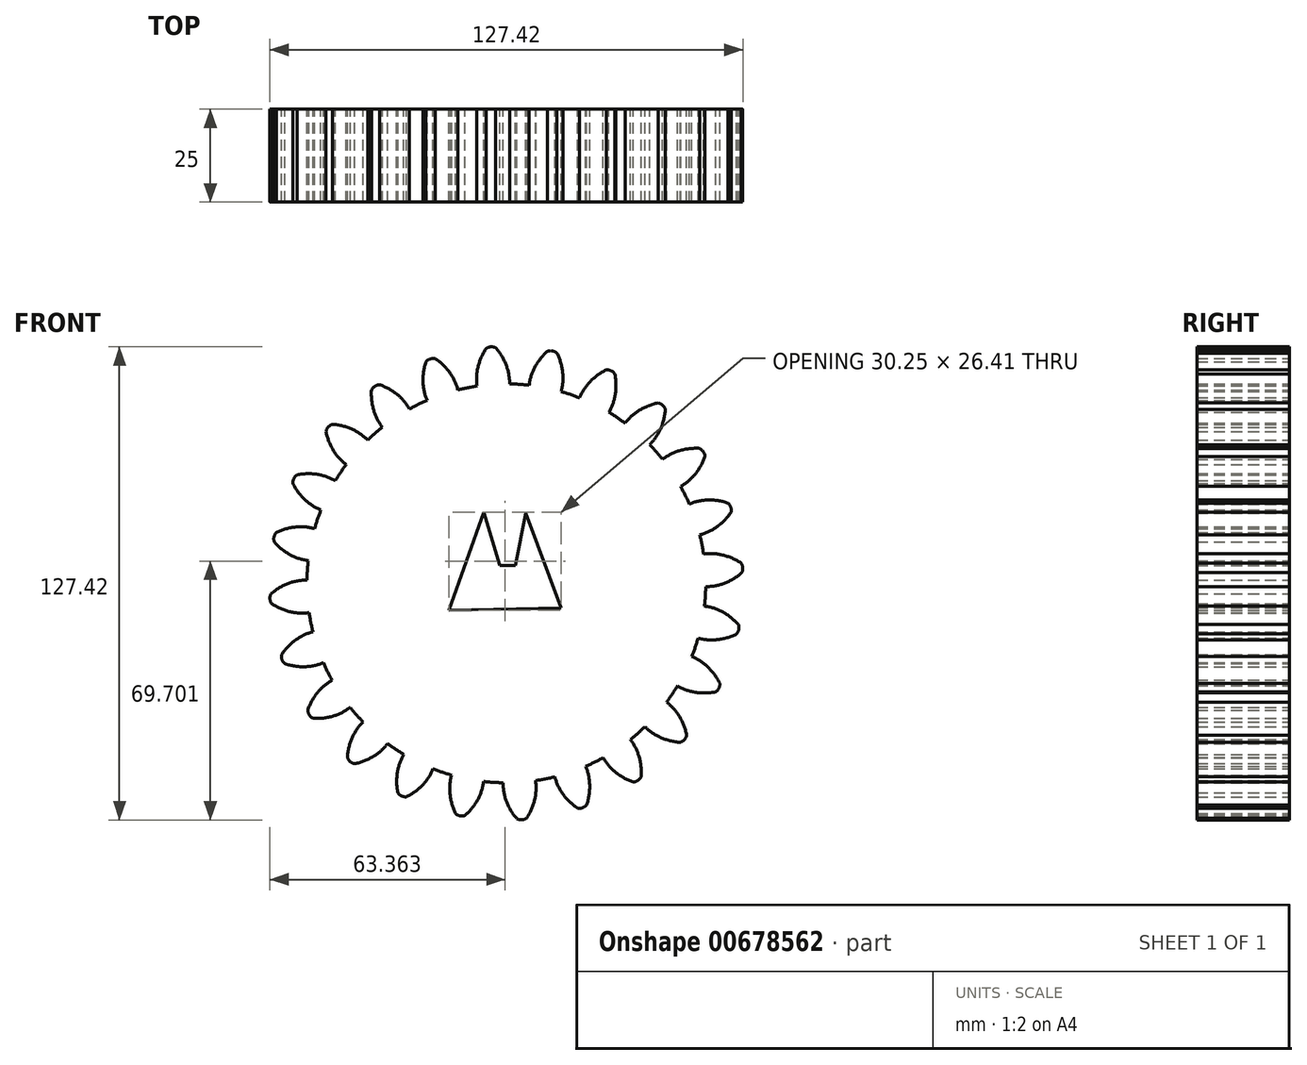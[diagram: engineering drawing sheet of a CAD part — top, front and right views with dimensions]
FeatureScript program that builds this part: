
annotation { "Feature Type Name" : "Feature", "Feature Type Description" : "" }
export const myFeature = defineFeature(function(context is Context, id is Id, definition is map)
    precondition{}
    {
        {
            var Q0;
            Q0=qCreatedBy(makeId("Front.planeOp"),FACE);
            var sketch = newSketch(context, id + "F0", { "sketchPlane" : qUnion([Q0])});
            skCircle(sketch, "E0", {"center": v(0, 0) * mm, "radius": 53.72 * mm});
            skCircle(sketch, "E1", {"center": v(0, 0) * mm, "radius": 58.67 * mm, "construction": true});
            skCircle(sketch, "E2", {"center": v(0, 0) * mm, "radius": 63.5 * mm, "construction": true});
            skLineSegment(sketch, "E3", {"start": v(0, 58.67) * mm, "end": v(-81.07, 58.67) * mm, "construction": true});
            skLineSegment(sketch, "E4", {"start": v(0, 58.67) * mm, "end": v(-75.05, 31.36) * mm, "construction": true});
            skCircle(sketch, "E5", {"center": v(0, 0) * mm, "radius": 55.14 * mm, "construction": true});
            skLineSegment(sketch, "E6", {"start": v(0, 0) * mm, "end": v(-5.28, 80.55) * mm, "construction": true});
            skLineSegment(sketch, "E7", {"start": v(0, 0) * mm, "end": v(0, 81.78) * mm, "construction": true});
            skCircle(sketch, "E8", {"center": v(0, 58.67) * mm, "radius": 14.6 * mm, "construction": true});
            skCircle(sketch, "E9", {"center": v(-13.72, 53.68) * mm, "radius": 14.6 * mm, "construction": true});
            skArc(sketch, "E10", {"start": v(0.88, 53.71) * mm, "mid": v(0.67, 56.23) * mm, "end": v(0, 58.67) * mm});
            skArc(sketch, "E11", {"start": v(0, 58.67) * mm, "mid": v(-1.22, 61.18) * mm, "end": v(-2.86, 63.44) * mm});
            skArc(sketch, "E12.MirrorCS", {"start": v(-7.66, 58.17) * mm, "mid": v(-6.78, 60.82) * mm, "end": v(-5.45, 63.27) * mm});
            skArc(sketch, "E13.MirrorCS", {"start": v(-7.88, 53.14) * mm, "mid": v(-8, 55.67) * mm, "end": v(-7.66, 58.17) * mm});
            skArc(sketch, "E14", {"start": v(-2.86, 63.44) * mm, "mid": v(-4.18, 63.7) * mm, "end": v(-5.45, 63.27) * mm});
            skLineSegment(sketch, "E15", {"start": v(0, 0) * mm, "end": v(0, -28.53) * mm, "construction": true});
            skLineSegment(sketch, "E16", {"start": v(-15.47, -7.21) * mm, "end": v(-6.12, 19.2) * mm});
            skLineSegment(sketch, "E17", {"start": v(-6.12, 19.2) * mm, "end": v(-1.72, 4.75) * mm});
            skLineSegment(sketch, "E18", {"start": v(-1.72, 4.75) * mm, "end": v(2.46, 4.75) * mm});
            skLineSegment(sketch, "E19", {"start": v(2.46, 4.75) * mm, "end": v(5.2, 18.88) * mm});
            skLineSegment(sketch, "E20", {"start": v(5.2, 18.88) * mm, "end": v(14.78, -6.58) * mm});
            skLineSegment(sketch, "E21", {"start": v(14.78, -6.58) * mm, "end": v(-15.47, -7.21) * mm});
            skSolve(sketch);
        }
        {
            var Q0;
            {var subQ0=sQuery(id+"F0.wireOp",EDGE,"AB84xeyR-P0go-5joV-o1QL-cVLlaDw5K9zT");Q0=makeQuery(id+"F0.imprint","IMPRINT",FACE,{"disambiguationData":[TD([[makeQuery(id+"F0.imprint","IMPRINT",EDGE,{"derivedFrom":subQ0}),1.0]])]});}
            var Q1;
            {var subQ6=sQuery(id+"F0.wireOp",EDGE,"E0");var subQ7=makeQuery(id+"F0.imprint","INTERSECT",VERTEX,{"derivedFrom":[subQ6,sQuery(id+"F0.wireOp",EDGE,"E10")]});Q1=makeQuery(id+"F0.imprint","IMPRINT",FACE,{"disambiguationData":[TD([[makeQuery(id+"F0.imprint","IMPRINT",EDGE,{"disambiguationData":[TD([[subQ7,-1.0]])],"derivedFrom":subQ6}),1.0]])]});}
            extrude(context, id + "F1", {"entities" : qUnion([Q0, Q1]), "depth" : 25 * mm, "offsetDistance" : 25 * mm});
        }
        {
            var Q0;
            {var subQ0=sQuery(id+"F0.wireOp",EDGE,"E10");Q0=makeQuery(id+"F0.imprint","IMPRINT",FACE,{"disambiguationData":[TD([[makeQuery(id+"F0.imprint","IMPRINT",EDGE,{"derivedFrom":subQ0}),1.0]])]});}
            extrude(context, id + "F2", {"entities" : qUnion([Q0]), "operationType" : NewBodyOperationType.ADD, "depth" : 25 * mm, "offsetDistance" : 25 * mm});
        }
        {
            var Q0;
            Q0=makeQuery(id+"F1.opExtrude","SWEPT_BODY",BODY,{"disambiguationData":[OSD([sQuery(id+"F0.wireOp",EDGE,"E0"),sQuery(id+"F0.wireOp",EDGE,"4qcLm8SV-9vJG-aGCV-NM1o-jUTKyLLJqKwo"),sQuery(id+"F0.wireOp",EDGE,"AB84xeyR-P0go-5joV-o1QL-cVLlaDw5K9zT"),sQuery(id+"F0.wireOp",EDGE,"21649afd-3bec-4f48-8976-60df220fce820.MirrorCS")])]});
            var Q1;
            Q1=makeQuery(id+"F1.opExtrude","SWEPT_FACE",FACE,{"disambiguationData":[OSD([sQuery(id+"F0.wireOp",EDGE,"E0")])]});
            circularPattern(context, id + "F3", {"operationType" : NewBodyOperationType.ADD, "entities" : qUnion([Q0]), "axis" : qUnion([Q1]), "angle" : 360 * degree, "instanceCount" : 24, "equalSpace" : true});
        }
        {
            var Q0;
            Q0=makeQuery(id+"F0.imprint","IMPRINT",FACE,{"disambiguationData":[TD([[makeQuery(id+"F0.imprint","IMPRINT",EDGE,{"derivedFrom":sQuery(id+"F0.wireOp",EDGE,"E16")}),-1.0]])]});
            extrude(context, id + "F4", {"entities" : qUnion([Q0]), "operationType" : NewBodyOperationType.REMOVE, "depth" : 54.2 * mm, "offsetDistance" : 25 * mm});
        }
    });
